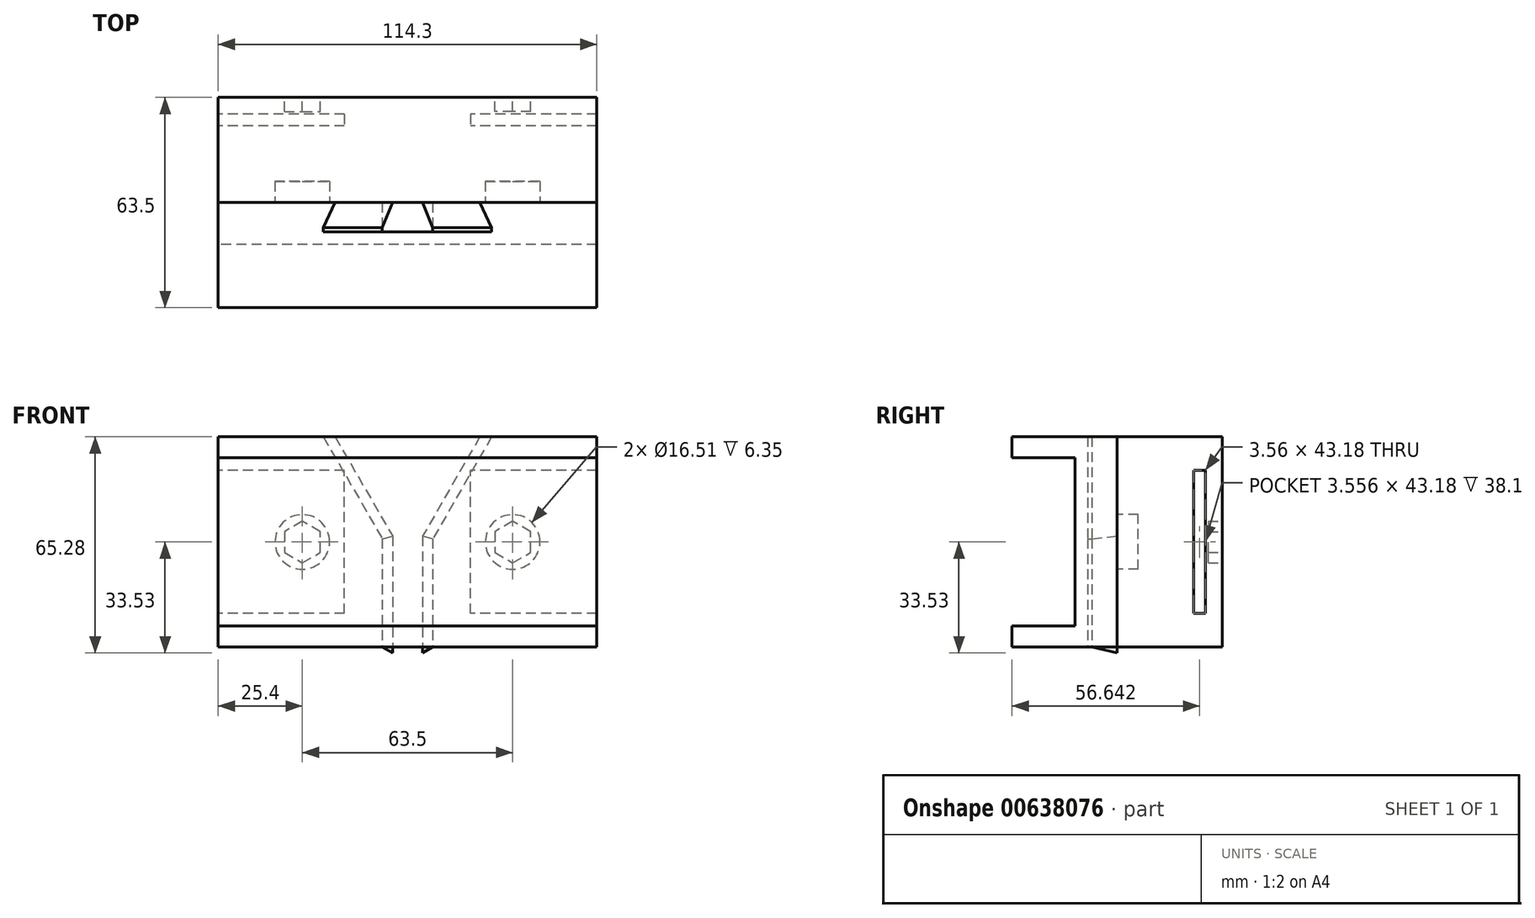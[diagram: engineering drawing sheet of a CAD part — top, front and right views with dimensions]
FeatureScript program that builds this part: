
annotation { "Feature Type Name" : "Feature", "Feature Type Description" : "" }
export const myFeature = defineFeature(function(context is Context, id is Id, definition is map)
    precondition{}
    {
        {
            var Q0;
            Q0=qCreatedBy(makeId("Right.planeOp"),FACE);
            var sketch = newSketch(context, id + "F0", { "sketchPlane" : qUnion([Q0])});
            skLineSegment(sketch, "E0", {"start": v(-26.95, -31.75) * mm, "end": v(36.55, -31.75) * mm});
            skLineSegment(sketch, "E1", {"start": v(36.55, 31.75) * mm, "end": v(-26.95, 31.75) * mm});
            skLineSegment(sketch, "E2", {"start": v(-26.95, 31.75) * mm, "end": v(-26.95, -31.75) * mm});
            skLineSegment(sketch, "E3", {"start": v(-26.95, 19.69) * mm, "end": v(-23.4, 19.69) * mm});
            skLineSegment(sketch, "E4", {"start": v(-23.4, 19.68) * mm, "end": v(-7.9, 8.89) * mm});
            skLineSegment(sketch, "E5", {"start": v(-7.9, 8.9) * mm, "end": v(-7.9, -8.9) * mm});
            skLineSegment(sketch, "E6", {"start": v(-7.9, -8.89) * mm, "end": v(-23.4, -19.68) * mm});
            skLineSegment(sketch, "E7", {"start": v(-23.4, -19.68) * mm, "end": v(-26.95, -19.68) * mm});
            skLineSegment(sketch, "E8.trimOffspring", {"start": v(36.55, -31.75) * mm, "end": v(36.55, 31.75) * mm});
            skLineSegment(sketch, "E9.trimOffspring", {"start": v(4.8, 31.75) * mm, "end": v(4.8, -31.75) * mm});
            skSolve(sketch);
        }
        {
            var Q0;
            {var subQ0=sQuery(id+"F0.wireOp",EDGE,"E8.trimOffspring");Q0=makeQuery(id+"F0.imprint","IMPRINT",FACE,{"disambiguationData":[TD([[makeQuery(id+"F0.imprint","IMPRINT",EDGE,{"derivedFrom":subQ0}),1.0]])]});}
            extrude(context, id + "F1", {"entities" : qUnion([Q0]), "depth" : 114.3 * mm, "offsetDistance" : 25.4 * mm});
        }
        {
            var Q0;
            {var subQ2=sQuery(id+"F0.wireOp",EDGE,"E3");Q0=makeQuery(id+"F0.imprint","IMPRINT",FACE,{"disambiguationData":[TD([[makeQuery(id+"F0.imprint","IMPRINT",EDGE,{"derivedFrom":subQ2}),1.0]])]});}
            var Q1;
            {var subQ0=sQuery(id+"F0.wireOp",EDGE,"E3");Q1=makeQuery(id+"F0.imprint","IMPRINT",FACE,{"disambiguationData":[TD([[makeQuery(id+"F0.imprint","IMPRINT",EDGE,{"derivedFrom":subQ0}),-1.0]])]});}
            extrude(context, id + "F2", {"entities" : qUnion([Q0, Q1]), "depth" : 114.3 * mm, "offsetDistance" : 25.4 * mm});
        }
        {
            var Q0;
            Q0=makeQuery(id+"F2.opExtrude","SWEPT_BODY",BODY,{"disambiguationData":[OSD([sQuery(id+"F0.wireOp",EDGE,"E0"),sQuery(id+"F0.wireOp",EDGE,"E1"),sQuery(id+"F0.wireOp",EDGE,"E2"),sQuery(id+"F0.wireOp",EDGE,"2Nn41NaE-Hgpe-s4fX-lzbf-wooGQdnGQ99G"),sQuery(id+"F0.wireOp",EDGE,"5qlYl4Ai-Fdpj-2xhL-xhdB-RVJ9mpbXSxHZ"),sQuery(id+"F0.wireOp",EDGE,"GVNRazZK-v03o-o9j3-2BiM-VDV5car0XNt5"),sQuery(id+"F0.wireOp",EDGE,"RzVRRZOU-TvBL-98Dw-26rr-Njfk6Q7A123n"),sQuery(id+"F0.wireOp",EDGE,"E9.trimOffspring")])]});
            deleteBodies(context, id + "F3", {"entities" : qUnion([Q0])});
        }
        {
            var Q0;
            Q0=makeQuery(id+"F1.opExtrude","SWEPT_FACE",FACE,{"disambiguationData":[OSD([sQuery(id+"F0.wireOp",EDGE,"E9.trimOffspring")])]});
            var sketch = newSketch(context, id + "F4", { "sketchPlane" : qUnion([Q0])});
            skLineSegment(sketch, "E10", {"start": v(57.15, 31.75) * mm, "end": v(57.15, -31.75) * mm});
            skLineSegment(sketch, "E11.0", {"start": v(31.75, 31.75) * mm, "end": v(49.53, 0.95) * mm});
            skLineSegment(sketch, "E12.0", {"start": v(-6.35, 38.1) * mm, "end": v(-6.35, -38.1) * mm});
            skLineSegment(sketch, "E12.1", {"start": v(120.65, 38.1) * mm, "end": v(-6.35, 38.1) * mm});
            skLineSegment(sketch, "E12.2", {"start": v(120.65, -38.1) * mm, "end": v(120.65, 38.1) * mm});
            skLineSegment(sketch, "E12.3", {"start": v(-6.35, -38.1) * mm, "end": v(120.65, -38.1) * mm});
            skLineSegment(sketch, "E13.0", {"start": v(82.55, 31.75) * mm, "end": v(64.77, 0.95) * mm});
            skLineSegment(sketch, "E14.0", {"start": v(49.53, 0.95) * mm, "end": v(49.53, -31.75) * mm});
            skLineSegment(sketch, "E15.0", {"start": v(64.77, 0.95) * mm, "end": v(64.77, -31.75) * mm});
            skPoint(sketch, "E16.orphan", {"position": v(50.8, -23.24) * mm});
            skSolve(sketch);
        }
        {
            var Q0;
            {var subQ0=sQuery(id+"F0.wireOp",EDGE,"E8.trimOffspring");Q0=makeQuery(id+"F0.imprint","IMPRINT",FACE,{"disambiguationData":[TD([[makeQuery(id+"F0.imprint","IMPRINT",EDGE,{"derivedFrom":subQ0}),1.0]])]});}
            var sketch = newSketch(context, id + "F5", { "sketchPlane" : qUnion([Q0])});
            skLineSegment(sketch, "E17.0", {"start": v(36.55, -31.75) * mm, "end": v(36.55, 31.75) * mm});
            skLineSegment(sketch, "E18.0", {"start": v(31.47, -21.59) * mm, "end": v(31.47, 21.6) * mm});
            skLineSegment(sketch, "E19.0", {"start": v(27.91, -21.59) * mm, "end": v(27.91, 21.6) * mm});
            skPoint(sketch, "E20.orphan", {"position": v(36.55, 0) * mm});
            skLineSegment(sketch, "E21.0", {"start": v(31.47, 21.6) * mm, "end": v(27.91, 21.6) * mm});
            skLineSegment(sketch, "E22.0", {"start": v(31.47, -21.59) * mm, "end": v(27.91, -21.59) * mm});
            skSolve(sketch);
        }
        {
            var Q0;
            Q0=makeQuery(id+"F5.imprint","IMPRINT",FACE,{"disambiguationData":[TD([[makeQuery(id+"F5.imprint","IMPRINT",EDGE,{"derivedFrom":sQuery(id+"F5.wireOp",EDGE,"E18.0")}),1.0]])]});
            extrude(context, id + "F6", {"entities" : qUnion([Q0]), "operationType" : NewBodyOperationType.REMOVE, "depth" : 38.1 * mm, "offsetDistance" : 25.4 * mm});
        }
        {
            var Q0;
            Q0=makeQuery(id+"F5.imprint","IMPRINT",FACE,{"disambiguationData":[TD([[makeQuery(id+"F5.imprint","IMPRINT",EDGE,{"derivedFrom":sQuery(id+"F5.wireOp",EDGE,"E18.0")}),1.0]])]});
            extrude(context, id + "F7", {"entities" : qUnion([Q0]), "operationType" : NewBodyOperationType.REMOVE, "depth" : 114.3 * mm, "offsetDistance" : 25.4 * mm, "hasSecondDirection" : true, "secondDirectionOppositeDirection" : false, "secondDirectionDepth" : 76.2 * mm});
        }
        {
            var Q0;
            {var subQ0=sQuery(id+"F0.wireOp",EDGE,"E1");Q0=makeQuery(id+"Fk5N4uHiYckjh5T_1.boolean.opBoolean","MERGE",FACE,{"derivedFrom":[makeQuery(id+"F1.opExtrude","SWEPT_FACE",FACE,{"disambiguationData":[OSD([subQ0])]}),makeQuery(id+"Fk5N4uHiYckjh5T_1.opExtrude","SWEPT_FACE",FACE,{"disambiguationData":[OSD([subQ0,sQuery(id+"F0.wireOp",EDGE,"E9.trimOffspring")])]})]});}
            var sketch = newSketch(context, id + "F8", { "sketchPlane" : qUnion([Q0])});
            skLineSegment(sketch, "E23", {"start": v(31.75, 4.8) * mm, "end": v(35.3, 4.8) * mm});
            skLineSegment(sketch, "E24", {"start": v(35.3, 4.8) * mm, "end": v(31.75, -2.82) * mm});
            skLineSegment(sketch, "E25", {"start": v(82.55, 4.8) * mm, "end": v(79, 4.8) * mm});
            skLineSegment(sketch, "E26", {"start": v(79, 4.8) * mm, "end": v(82.55, -2.82) * mm});
            skLineSegment(sketch, "E27", {"start": v(31.75, 4.8) * mm, "end": v(31.75, -2.82) * mm});
            skLineSegment(sketch, "E28", {"start": v(82.55, 4.8) * mm, "end": v(82.55, -2.82) * mm});
            skSolve(sketch);
        }
        {
            var Q0;
            Q0=makeQuery(id+"F8.imprint","IMPRINT",FACE,{"disambiguationData":[TD([[makeQuery(id+"F8.imprint","IMPRINT",EDGE,{"derivedFrom":sQuery(id+"F8.wireOp",EDGE,"E23")}),1.0]])]});
            var Q1;
            Q1=sQuery(id+"F4.wireOp",EDGE,"E14.0");
            var Q2;
            Q2=sQuery(id+"F4.wireOp",EDGE,"E11.0");
            sweep(context, id + "F9", {"profiles" : qUnion([Q0]), "path" : qUnion([Q1, Q2])});
        }
        {
            var Q0;
            Q0=makeQuery(id+"F8.imprint","IMPRINT",FACE,{"disambiguationData":[TD([[makeQuery(id+"F8.imprint","IMPRINT",EDGE,{"derivedFrom":sQuery(id+"F8.wireOp",EDGE,"E25")}),1.0]])]});
            var Q1;
            Q1=sQuery(id+"F4.wireOp",EDGE,"E13.0");
            var Q2;
            Q2=sQuery(id+"F4.wireOp",EDGE,"E15.0");
            sweep(context, id + "F10", {"profiles" : qUnion([Q0]), "path" : qUnion([Q1, Q2])});
        }
        {
            var Q0;
            {var subQ0=sQuery(id+"F4.wireOp",EDGE,"E11.0");var subQ2=sQuery(id+"F0.wireOp",EDGE,"E9.trimOffspring");var subQ3=makeQuery(id+"F1.opExtrude","SWEPT_FACE",FACE,{"disambiguationData":[OSD([subQ2])]});Q0=makeQuery(id+"F9.boolean.opBoolean","MERGE",FACE,{"derivedFrom":[makeQuery(id+"Fk5N4uHiYckjh5T_1.boolean.opBoolean","SPLIT",FACE,{"disambiguationData":[TD([makeQuery(id+"Fk5N4uHiYckjh5T_1.opExtrude","SWEPT_FACE",FACE,{"disambiguationData":[OSD([subQ0])]})])],"derivedFrom":subQ3}),makeQuery(id+"F9.opSweep","SWEPT_FACE",FACE,{"disambiguationData":[OSD([subQ0,sQuery(id+"F8.wireOp",EDGE,"E23")])]})]});}
            var sketch = newSketch(context, id + "F11", { "sketchPlane" : qUnion([Q0])});
            skCircle(sketch, "E29", {"center": v(25.4, 0) * mm, "radius": 8.26 * mm});
            skSolve(sketch);
        }
        {
            var Q0;
            {var subQ0=sQuery(id+"F4.wireOp",EDGE,"E13.0");var subQ3=sQuery(id+"F0.wireOp",EDGE,"E9.trimOffspring");var subQ4=makeQuery(id+"F1.opExtrude","SWEPT_FACE",FACE,{"disambiguationData":[OSD([subQ3])]});Q0=makeQuery(id+"F10.boolean.opBoolean","MERGE",FACE,{"derivedFrom":[makeQuery(id+"Fk5N4uHiYckjh5T_1.boolean.opBoolean","SPLIT",FACE,{"disambiguationData":[TD([makeQuery(id+"Fk5N4uHiYckjh5T_1.opExtrude","SWEPT_FACE",FACE,{"disambiguationData":[OSD([subQ0])]})])],"derivedFrom":subQ4}),makeQuery(id+"F10.opSweep","SWEPT_FACE",FACE,{"disambiguationData":[OSD([subQ0,sQuery(id+"F8.wireOp",EDGE,"E25")])]})]});}
            var sketch = newSketch(context, id + "F12", { "sketchPlane" : qUnion([Q0])});
            skCircle(sketch, "E30", {"center": v(88.9, 0) * mm, "radius": 8.26 * mm});
            skSolve(sketch);
        }
        {
            var Q0;
            Q0=makeQuery(id+"F11.imprint","IMPRINT",FACE,{"disambiguationData":[TD([[makeQuery(id+"F11.imprint","IMPRINT",EDGE,{"derivedFrom":sQuery(id+"F11.wireOp",EDGE,"E29")}),1.0]])]});
            var Q1;
            Q1=makeQuery(id+"F12.imprint","IMPRINT",FACE,{"disambiguationData":[TD([[makeQuery(id+"F12.imprint","IMPRINT",EDGE,{"derivedFrom":sQuery(id+"F12.wireOp",EDGE,"E30")}),1.0]])]});
            extrude(context, id + "F13", {"entities" : qUnion([Q0, Q1]), "operationType" : NewBodyOperationType.REMOVE, "oppositeDirection" : true, "depth" : 6.35 * mm, "offsetDistance" : 25.4 * mm});
        }
        {
            var Q0;
            Q0=makeQuery(id+"F1.opExtrude","SWEPT_FACE",FACE,{"disambiguationData":[OSD([sQuery(id+"F0.wireOp",EDGE,"E8.trimOffspring")])]});
            var sketch = newSketch(context, id + "F14", { "sketchPlane" : qUnion([Q0])});
            skCircle(sketch, "E31.cCircle", {"center": v(-88.9, 0) * mm, "radius": 5.44 * mm, "construction": true});
            skLineSegment(sketch, "E31.0", {"start": v(-83.46, 3.14) * mm, "end": v(-83.46, -3.14) * mm});
            skLineSegment(sketch, "E31.1", {"start": v(-83.46, -3.14) * mm, "end": v(-88.9, -6.28) * mm});
            skLineSegment(sketch, "E31.2", {"start": v(-88.9, -6.28) * mm, "end": v(-94.34, -3.14) * mm});
            skLineSegment(sketch, "E31.3", {"start": v(-94.34, -3.14) * mm, "end": v(-94.34, 3.14) * mm});
            skLineSegment(sketch, "E31.4", {"start": v(-94.34, 3.14) * mm, "end": v(-88.9, 6.28) * mm});
            skLineSegment(sketch, "E31.5", {"start": v(-88.9, 6.28) * mm, "end": v(-83.46, 3.14) * mm});
            skPoint(sketch, "E31.0.midPoint", {"position": v(-83.46, 0) * mm});
            skCircle(sketch, "E32.cCircle", {"center": v(-25.4, 0) * mm, "radius": 5.44 * mm, "construction": true});
            skLineSegment(sketch, "E32.0", {"start": v(-30.84, -3.14) * mm, "end": v(-30.84, 3.14) * mm});
            skLineSegment(sketch, "E32.1", {"start": v(-30.84, 3.14) * mm, "end": v(-25.4, 6.28) * mm});
            skLineSegment(sketch, "E32.2", {"start": v(-25.4, 6.28) * mm, "end": v(-19.96, 3.14) * mm});
            skLineSegment(sketch, "E32.3", {"start": v(-19.96, 3.14) * mm, "end": v(-19.96, -3.14) * mm});
            skLineSegment(sketch, "E32.4", {"start": v(-19.96, -3.14) * mm, "end": v(-25.4, -6.28) * mm});
            skLineSegment(sketch, "E32.5", {"start": v(-25.4, -6.28) * mm, "end": v(-30.84, -3.14) * mm});
            skPoint(sketch, "E32.0.midPoint", {"position": v(-30.84, 0) * mm});
            skSolve(sketch);
        }
        {
            var Q0;
            Q0=makeQuery(id+"F14.imprint","IMPRINT",FACE,{"disambiguationData":[TD([[makeQuery(id+"F14.imprint","IMPRINT",EDGE,{"derivedFrom":sQuery(id+"F14.wireOp",EDGE,"E31.0")}),-1.0]])]});
            var Q1;
            Q1=makeQuery(id+"F14.imprint","IMPRINT",FACE,{"disambiguationData":[TD([[makeQuery(id+"F14.imprint","IMPRINT",EDGE,{"derivedFrom":sQuery(id+"F14.wireOp",EDGE,"E32.0")}),-1.0]])]});
            extrude(context, id + "F15", {"entities" : qUnion([Q0, Q1]), "operationType" : NewBodyOperationType.REMOVE, "oppositeDirection" : true, "depth" : 4.27 * mm, "offsetDistance" : 25.4 * mm});
        }
        {
            var Q0;
            {var subQ3=sQuery(id+"F4.wireOp",EDGE,"E11.0");Q0=makeQuery(id+"F4.imprint","IMPRINT",FACE,{"disambiguationData":[TD([[makeQuery(id+"F4.imprint","IMPRINT",EDGE,{"derivedFrom":subQ3}),-1.0]])]});}
            var Q1;
            {var subQ3=sQuery(id+"F4.wireOp",EDGE,"E13.0");Q1=makeQuery(id+"F4.imprint","IMPRINT",FACE,{"disambiguationData":[TD([[makeQuery(id+"F4.imprint","IMPRINT",EDGE,{"derivedFrom":subQ3}),1.0]])]});}
            extrude(context, id + "F16", {"entities" : qUnion([Q0, Q1]), "depth" : 25.4 * mm, "offsetDistance" : 25.4 * mm});
        }
        {
            var Q0;
            {var subQ2=sQuery(id+"F4.wireOp",EDGE,"E10");Q0=makeQuery(id+"F4.imprint","IMPRINT",FACE,{"disambiguationData":[TD([[makeQuery(id+"F4.imprint","IMPRINT",EDGE,{"derivedFrom":subQ2}),-1.0]])]});}
            var Q1;
            {var subQ0=sQuery(id+"F4.wireOp",EDGE,"E10");Q1=makeQuery(id+"F4.imprint","IMPRINT",FACE,{"disambiguationData":[TD([[makeQuery(id+"F4.imprint","IMPRINT",EDGE,{"derivedFrom":subQ0}),1.0]])]});}
            extrude(context, id + "F17", {"entities" : qUnion([Q0, Q1]), "depth" : 25.4 * mm, "offsetDistance" : 25.4 * mm, "hasSecondDirection" : true, "secondDirectionOppositeDirection" : true, "secondDirectionDepth" : -8.9 * mm});
        }
        {
            var Q0;
            Q0=makeQuery(id+"F9.opSweep","SWEPT_BODY",BODY,{"disambiguationData":[OSD([sQuery(id+"F4.wireOp",EDGE,"E11.0"),sQuery(id+"F8.wireOp",EDGE,"E23"),sQuery(id+"F8.wireOp",EDGE,"E24"),sQuery(id+"F8.wireOp",EDGE,"E27")])]});
            var Q1;
            Q1=makeQuery(id+"F10.opSweep","SWEPT_BODY",BODY,{"disambiguationData":[OSD([sQuery(id+"F4.wireOp",EDGE,"E15.0"),sQuery(id+"F8.wireOp",EDGE,"E25"),sQuery(id+"F8.wireOp",EDGE,"E26"),sQuery(id+"F8.wireOp",EDGE,"E28")])]});
            var Q2;
            Q2=makeQuery(id+"F16.opExtrude","SWEPT_BODY",BODY,{"disambiguationData":[OSD([sQuery(id+"F0.wireOp",EDGE,"E0"),sQuery(id+"F0.wireOp",EDGE,"E1"),sQuery(id+"F0.wireOp",EDGE,"E9.trimOffspring"),sQuery(id+"FQNvP4g6ZDJs9w2_2.hole-0.sketch.wireOp",EDGE,"core_line_2"),sQuery(id+"F4.wireOp",EDGE,"E11.0"),sQuery(id+"F4.wireOp",EDGE,"E14.0")])]});
            var Q3;
            Q3=makeQuery(id+"F16.opExtrude","SWEPT_BODY",BODY,{"disambiguationData":[OSD([sQuery(id+"F0.wireOp",EDGE,"E0"),sQuery(id+"F0.wireOp",EDGE,"E1"),sQuery(id+"F0.wireOp",EDGE,"E9.trimOffspring"),sQuery(id+"FQNvP4g6ZDJs9w2_2.hole-1.sketch.wireOp",EDGE,"core_line_2"),sQuery(id+"F4.wireOp",EDGE,"E13.0"),sQuery(id+"F4.wireOp",EDGE,"E15.0")])]});
            var Q4;
            Q4=makeQuery(id+"F17.opExtrude","SWEPT_BODY",BODY,{"disambiguationData":[OSD([sQuery(id+"F0.wireOp",EDGE,"E0"),sQuery(id+"F0.wireOp",EDGE,"E1"),sQuery(id+"F0.wireOp",EDGE,"E9.trimOffspring"),sQuery(id+"F4.wireOp",EDGE,"E11.0"),sQuery(id+"F4.wireOp",EDGE,"E13.0"),sQuery(id+"F4.wireOp",EDGE,"E14.0"),sQuery(id+"F4.wireOp",EDGE,"E15.0")])]});
            booleanBodies(context, id + "F18", {"operationType" : BooleanOperationType.UNION, "tools" : qUnion([Q0, Q1, Q2, Q3, Q4])});
        }
        {
            var Q0;
            {var subQ0=sQuery(id+"F4.wireOp",EDGE,"E15.0");var subQ1=sQuery(id+"F4.wireOp",EDGE,"E14.0");var subQ2=sQuery(id+"F4.wireOp",EDGE,"E13.0");var subQ3=sQuery(id+"F4.wireOp",EDGE,"E11.0");var subQ4=sQuery(id+"F0.wireOp",EDGE,"E9.trimOffspring");var subQ5=sQuery(id+"F0.wireOp",EDGE,"E1");var subQ6=sQuery(id+"F0.wireOp",EDGE,"E0");Q0=makeQuery(id+"F18.opBoolean","MERGE",FACE,{"derivedFrom":[makeQuery(id+"F16.opExtrude","CAP_FACE",FACE,{"disambiguationData":[OSD([subQ6,subQ5,subQ4,sQuery(id+"FQNvP4g6ZDJs9w2_2.hole-0.sketch.wireOp",EDGE,"core_line_2"),subQ3,subQ1])],"isStart":false}),makeQuery(id+"F16.opExtrude","CAP_FACE",FACE,{"disambiguationData":[OSD([subQ6,subQ5,subQ4,sQuery(id+"FQNvP4g6ZDJs9w2_2.hole-1.sketch.wireOp",EDGE,"core_line_2"),subQ2,subQ0])],"isStart":false}),makeQuery(id+"F17.opExtrude","CAP_FACE",FACE,{"disambiguationData":[OSD([subQ6,subQ5,subQ4,subQ3,subQ2,subQ1,subQ0])],"isStart":false})]});}
            var sketch = newSketch(context, id + "F19", { "sketchPlane" : qUnion([Q0])});
            skLineSegment(sketch, "E33.0", {"start": v(114.3, -15.24) * mm, "end": v(0, -15.24) * mm});
            skLineSegment(sketch, "E34.0", {"start": v(114.3, 15.24) * mm, "end": v(0, 15.24) * mm});
            skLineSegment(sketch, "E35", {"start": v(114.3, -15.24) * mm, "end": v(114.3, 15.24) * mm});
            skLineSegment(sketch, "E36", {"start": v(0, -15.24) * mm, "end": v(0, 15.24) * mm});
            skSolve(sketch);
        }
        {
            var Q0;
            Q0=makeQuery(id+"F19.imprint","IMPRINT",FACE,{"disambiguationData":[TD([[makeQuery(id+"F19.imprint","IMPRINT",EDGE,{"derivedFrom":sQuery(id+"F19.wireOp",EDGE,"E33.0")}),-1.0]])]});
            extrude(context, id + "F20", {"entities" : qUnion([Q0]), "operationType" : NewBodyOperationType.REMOVE, "oppositeDirection" : true, "depth" : 12.7 * mm, "offsetDistance" : 25.4 * mm, "hasSecondDirection" : true, "secondDirectionOppositeDirection" : true, "secondDirectionDepth" : 7.62 * mm});
        }
        {
            var Q0;
            {var subQ6=sQuery(id+"F0.wireOp",EDGE,"E3");Q0=makeQuery(id+"F0.imprint","IMPRINT",FACE,{"disambiguationData":[TD([[makeQuery(id+"F0.imprint","IMPRINT",EDGE,{"derivedFrom":subQ6}),1.0]])]});}
            var sketch = newSketch(context, id + "F21", { "sketchPlane" : qUnion([Q0])});
            skLineSegment(sketch, "E37.0", {"start": v(4.8, 31.75) * mm, "end": v(4.8, -31.75) * mm});
            skLineSegment(sketch, "E38.0", {"start": v(-46, 31.75) * mm, "end": v(-46, 25.4) * mm});
            skLineSegment(sketch, "E39", {"start": v(-7.9, 31.75) * mm, "end": v(-46, 31.75) * mm});
            skLineSegment(sketch, "E40", {"start": v(-7.9, -31.75) * mm, "end": v(-46, -31.75) * mm});
            skLineSegment(sketch, "E41.0", {"start": v(-7.9, -25.4) * mm, "end": v(-46, -25.4) * mm});
            skLineSegment(sketch, "E42.0", {"start": v(-7.9, 25.4) * mm, "end": v(-46, 25.4) * mm});
            skLineSegment(sketch, "E43.0", {"start": v(-7.9, 31.75) * mm, "end": v(-7.9, 25.4) * mm});
            skLineSegment(sketch, "E44.trimOffspring", {"start": v(-7.9, -25.4) * mm, "end": v(-7.9, -31.75) * mm});
            skLineSegment(sketch, "E45.trimOffspring", {"start": v(-46, -25.4) * mm, "end": v(-46, -31.75) * mm});
            skSolve(sketch);
        }
        {
            var Q0;
            {var subQ2=sQuery(id+"F21.wireOp",EDGE,"E37.0");Q0=makeQuery(id+"F21.imprint","IMPRINT",FACE,{"disambiguationData":[TD([[makeQuery(id+"F21.imprint","IMPRINT",EDGE,{"derivedFrom":subQ2}),-1.0]])]});}
            var sketch = newSketch(context, id + "F22", { "sketchPlane" : qUnion([Q0])});
            skLineSegment(sketch, "E46.0", {"start": v(-20.6, 31.75) * mm, "end": v(-20.6, -31.75) * mm});
            skLineSegment(sketch, "E47.0", {"start": v(4.8, 31.75) * mm, "end": v(4.8, -31.75) * mm});
            skLineSegment(sketch, "E48.0", {"start": v(-7.9, 31.75) * mm, "end": v(-7.9, -31.75) * mm});
            skLineSegment(sketch, "E49", {"start": v(-7.9, 31.75) * mm, "end": v(-20.6, 31.75) * mm});
            skLineSegment(sketch, "E50", {"start": v(-7.9, -31.75) * mm, "end": v(-20.6, -31.75) * mm});
            skSolve(sketch);
        }
        {
            var Q0;
            {var subQ5=makeQuery(id+"F21.imprint","IMPRINT",EDGE,{"derivedFrom":makeQuery(id+"F0.imprint","IMPRINT",EDGE,{"derivedFrom":sQuery(id+"F0.wireOp",EDGE,"E4")})});var subQ7=sQuery(id+"F22.wireOp",EDGE,"E48.0");var subQ8=makeQuery(id+"F22.imprint","INTERSECT",VERTEX,{"derivedFrom":[subQ5,subQ7]});Q0=makeQuery(id+"F22.imprint","IMPRINT",FACE,{"disambiguationData":[TD([[makeQuery(id+"F22.imprint","IMPRINT",EDGE,{"disambiguationData":[TD([[subQ8,1.0]])],"derivedFrom":subQ5}),1.0]])]});}
            var Q1;
            {var subQ0=sQuery(id+"F22.wireOp",EDGE,"E49");Q1=makeQuery(id+"F22.imprint","IMPRINT",FACE,{"disambiguationData":[TD([[makeQuery(id+"F22.imprint","IMPRINT",EDGE,{"derivedFrom":subQ0}),1.0]])]});}
            var Q2;
            {var subQ0=sQuery(id+"F22.wireOp",EDGE,"E46.0");var subQ1=makeQuery(id+"F21.imprint","IMPRINT",EDGE,{"derivedFrom":makeQuery(id+"F0.imprint","IMPRINT",EDGE,{"derivedFrom":sQuery(id+"F0.wireOp",EDGE,"E4")})});var subQ2=makeQuery(id+"F22.imprint","INTERSECT",VERTEX,{"derivedFrom":[subQ1,subQ0]});Q2=makeQuery(id+"F22.imprint","IMPRINT",FACE,{"disambiguationData":[TD([[makeQuery(id+"F22.imprint","IMPRINT",EDGE,{"disambiguationData":[TD([[subQ2,-1.0]])],"derivedFrom":subQ0}),1.0]])]});}
            var Q3;
            {var subQ1=makeQuery(id+"F21.imprint","IMPRINT",EDGE,{"derivedFrom":makeQuery(id+"F0.imprint","IMPRINT",EDGE,{"derivedFrom":sQuery(id+"F0.wireOp",EDGE,"E6")})});var subQ7=sQuery(id+"F22.wireOp",EDGE,"E48.0");var subQ8=makeQuery(id+"F22.imprint","INTERSECT",VERTEX,{"derivedFrom":[subQ1,subQ7]});Q3=makeQuery(id+"F22.imprint","IMPRINT",FACE,{"disambiguationData":[TD([[makeQuery(id+"F22.imprint","IMPRINT",EDGE,{"disambiguationData":[TD([[subQ8,-1.0]])],"derivedFrom":subQ1}),1.0]])]});}
            var Q4;
            {var subQ0=sQuery(id+"F22.wireOp",EDGE,"E50");Q4=makeQuery(id+"F22.imprint","IMPRINT",FACE,{"disambiguationData":[TD([[makeQuery(id+"F22.imprint","IMPRINT",EDGE,{"derivedFrom":subQ0}),-1.0]])]});}
            extrude(context, id + "F23", {"entities" : qUnion([Q0, Q1, Q2, Q3, Q4]), "operationType" : NewBodyOperationType.REMOVE, "depth" : 114.3 * mm, "offsetDistance" : 25.4 * mm});
        }
        {
            var Q0;
            {var subQ6=sQuery(id+"F21.wireOp",EDGE,"E43.0");Q0=makeQuery(id+"F21.imprint","IMPRINT",FACE,{"disambiguationData":[TD([[makeQuery(id+"F21.imprint","IMPRINT",EDGE,{"derivedFrom":subQ6}),-1.0]])]});}
            var Q1;
            {var subQ6=sQuery(id+"F21.wireOp",EDGE,"E44.trimOffspring");Q1=makeQuery(id+"F21.imprint","IMPRINT",FACE,{"disambiguationData":[TD([[makeQuery(id+"F21.imprint","IMPRINT",EDGE,{"derivedFrom":subQ6}),-1.0]])]});}
            extrude(context, id + "F24", {"entities" : qUnion([Q0, Q1]), "operationType" : NewBodyOperationType.ADD, "depth" : 114.3 * mm, "offsetDistance" : 25.4 * mm});
        }
    });
